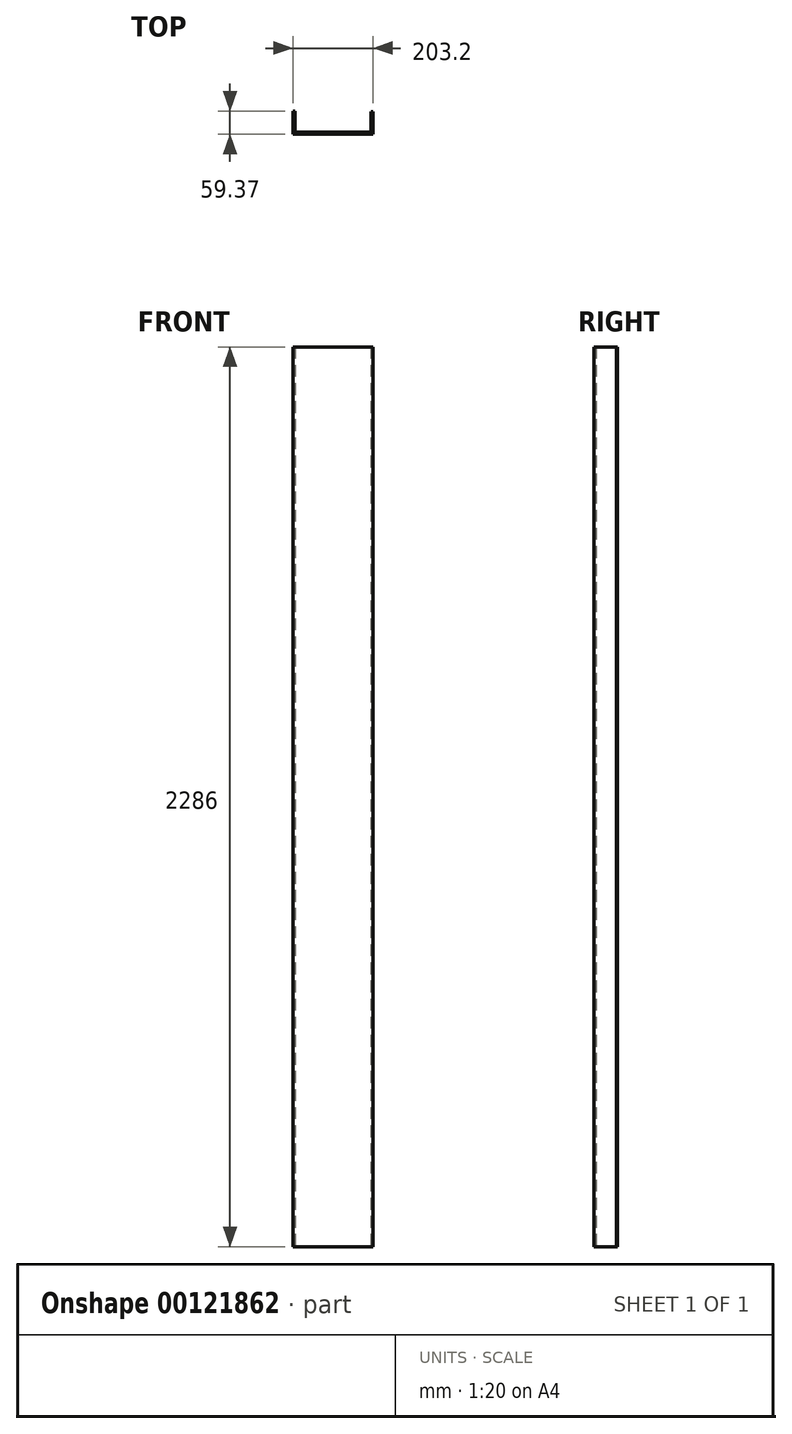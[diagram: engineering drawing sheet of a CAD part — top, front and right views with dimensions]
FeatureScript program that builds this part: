
annotation { "Feature Type Name" : "Feature", "Feature Type Description" : "" }
export const myFeature = defineFeature(function(context is Context, id is Id, definition is map)
    precondition{}
    {
        {
            var Q0;
            Q0=qCreatedBy(makeId("Top.planeOp"),FACE);
            var sketch = newSketch(context, id + "F0", { "sketchPlane" : qUnion([Q0])});
            skLineSegment(sketch, "E0", {"start": v(-100.05, 0) * mm, "end": v(103.15, 0) * mm});
            skLineSegment(sketch, "E1", {"start": v(103.15, 0) * mm, "end": v(103.15, 57.4) * mm});
            skLineSegment(sketch, "E2", {"start": v(103.15, 57.4) * mm, "end": v(97.57, 57.4) * mm});
            skLineSegment(sketch, "E3", {"start": v(97.57, 57.4) * mm, "end": v(97.57, 5.59) * mm});
            skLineSegment(sketch, "E4", {"start": v(97.57, 5.59) * mm, "end": v(-94.46, 5.59) * mm});
            skLineSegment(sketch, "E5", {"start": v(-94.46, 5.59) * mm, "end": v(-94.46, 59.37) * mm});
            skLineSegment(sketch, "E6", {"start": v(-94.46, 59.37) * mm, "end": v(-100.05, 59.37) * mm});
            skLineSegment(sketch, "E7", {"start": v(-100.05, 59.37) * mm, "end": v(-100.05, 0) * mm});
            skSolve(sketch);
        }
        {
            var Q0;
            Q0 = qSketchRegion(id + "F0", true);
            extrude(context, id + "F1", {"entities" : qUnion([Q0]), "depth" : 2286 * mm});
        }
    });
